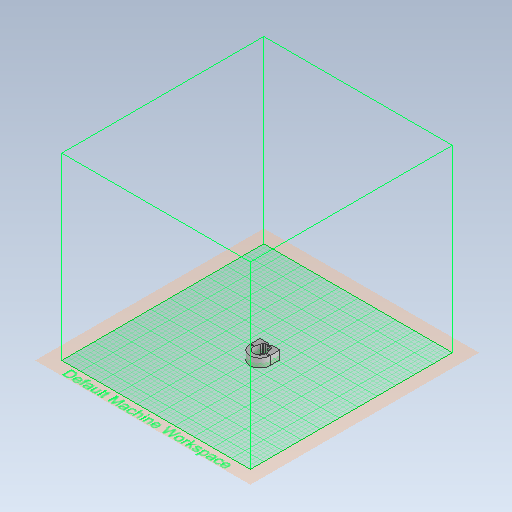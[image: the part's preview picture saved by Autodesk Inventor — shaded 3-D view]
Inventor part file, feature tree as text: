
AUTODESK INVENTOR PART (.ipt)
format: ipt  version: 2021 (Build 250183000, 183)  size: 419,328 bytes
history: native  units: mm
features: sketch x9, extrude x9, fillet x3, other x1
ambient origin geometry x8: Origin, YZ Plane, XZ Plane, XY Plane, X Axis, Y Axis, Z Axis, Center Point
bodies: Body1 (feature_tree)
feature tree (22):
  other  "Fahrwerk_motorhalterung"
  sketch  "Skizze1"  dims[d2=3.5mm d3=3.5mm]
  extrude  "Extrusion2"  Depth=3.5mm
  extrude  "Extrusion3"  Depth=44.5mm
  extrude  "Extrusion4"  Depth=3.0mm
  fillet  "Rundung1"  Radius=19.0mm
  sketch  "Skizze4"  dims[d15=7.0mm d16=11.4mm]
  fillet  "Rundung2"  Radius=17.0mm
  extrude  "Extrusion7"  Depth=11.4mm
  extrude  "Extrusion8"  Depth=5.5mm
  extrude  "Extrusion9"  Depth=3.0mm TaperAngle=0.0deg
  sketch  "Skizze8"  dims[d23=2.0mm d32=1.0mm]
  extrude  "Extrusion11"  Depth=1.0mm
  extrude  "Extrusion12"  Depth=5.75mm
  extrude  "Extrusion13"  Depth=13.0mm
  fillet  "Rundung6"  Radius=10.0mm
  sketch  "Skizze2"  dims[d8=28.5mm d9=44.5mm]
  sketch  "Skizze3"  dims[d10=44.5mm d11=3.0mm d12=19.0mm d13=0.0mm d14=17.0mm]
  sketch  "Skizze5"  dims[d17=19.0mm d18=0.0mm d19=5.5mm]
  sketch  "Skizze6"  dims[d20=3.0mm d21=4.0mm d22=0.0mm]
  sketch  "Skizze9"  dims[d34=1.5mm d38=5.75mm]
  sketch  "Skizze10"  dims[d39=9.8mm d45=4.5mm d46=10.0mm d48=1.5mm d49=15.0mm d50=0.0mm d51=13.0mm d52=3.0mm d53=0.0mm d54=10.0mm d55=6.0mm d56=0.0mm d60=6.5mm d61=2.0mm d62=7.8mm d63=11.0mm d64=0.0mm d65=4.5mm d66=6.0mm d67=0.0mm d68=18.0mm d69=0.0mm d70=13.0mm]
